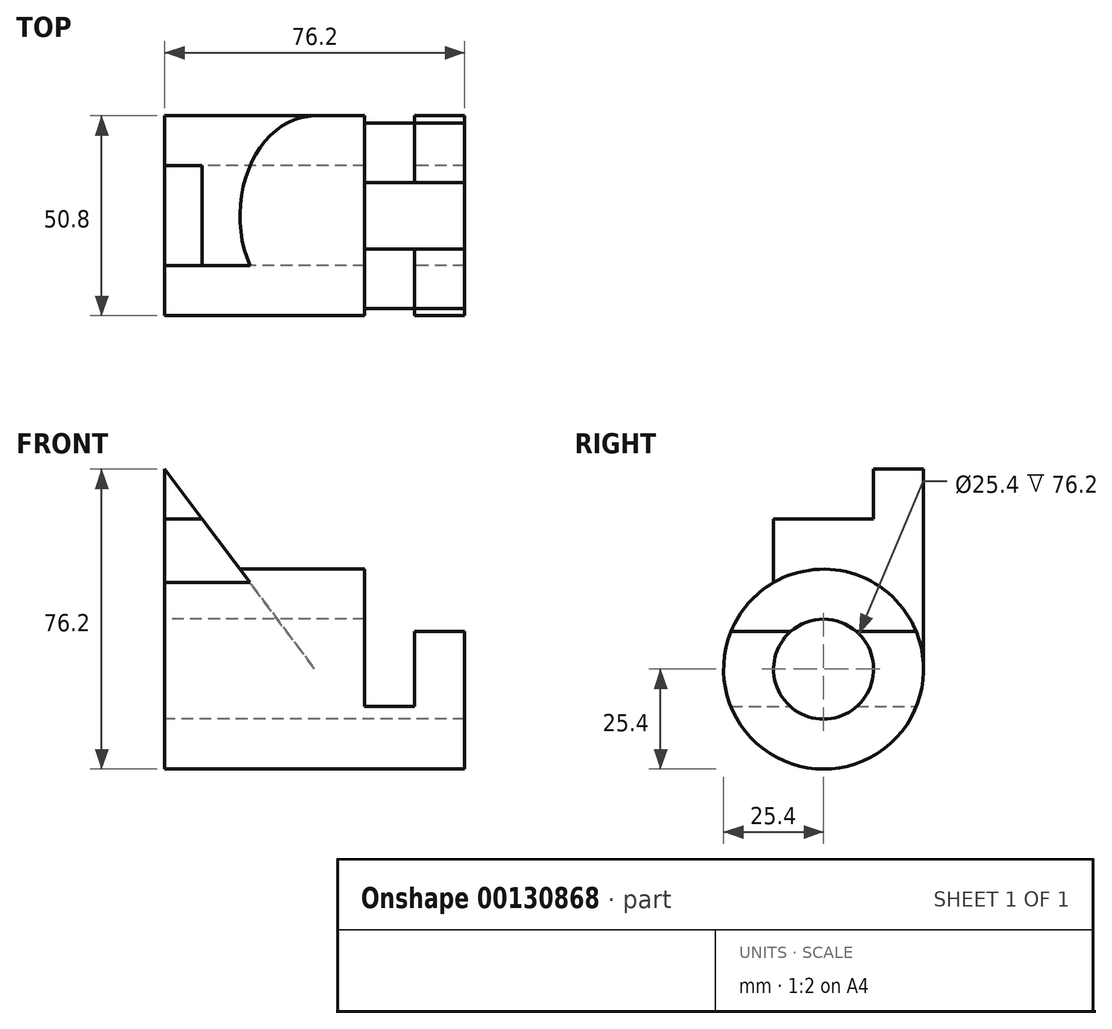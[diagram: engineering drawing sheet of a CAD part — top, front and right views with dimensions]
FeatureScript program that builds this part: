
annotation { "Feature Type Name" : "Feature", "Feature Type Description" : "" }
export const myFeature = defineFeature(function(context is Context, id is Id, definition is map)
    precondition{}
    {
        {
            var Q0;
            Q0=qCreatedBy(makeId("Right.planeOp"),FACE);
            var sketch = newSketch(context, id + "F0", { "sketchPlane" : qUnion([Q0])});
            skCircle(sketch, "E0", {"center": v(0, 0) * mm, "radius": 12.7 * mm});
            skCircle(sketch, "E1", {"center": v(0, 0) * mm, "radius": 25.4 * mm});
            skSolve(sketch);
        }
        {
            var Q0;
            Q0=qCreatedBy(makeId("Front.planeOp"),FACE);
            var sketch = newSketch(context, id + "F1", { "sketchPlane" : qUnion([Q0])});
            skLineSegment(sketch, "E2", {"start": v(0, 0) * mm, "end": v(0, 25.4) * mm, "construction": true});
            skLineSegment(sketch, "E3", {"start": v(0, 25.4) * mm, "end": v(50.8, 25.4) * mm, "construction": true});
            skLineSegment(sketch, "E4", {"start": v(50.8, 25.4) * mm, "end": v(50.8, -9.53) * mm});
            skLineSegment(sketch, "E5", {"start": v(50.8, -9.53) * mm, "end": v(63.5, -9.53) * mm});
            skLineSegment(sketch, "E6", {"start": v(63.5, -9.53) * mm, "end": v(63.5, 25.4) * mm});
            skLineSegment(sketch, "E7", {"start": v(63.5, 25.4) * mm, "end": v(50.8, 25.4) * mm});
            skSolve(sketch);
        }
        {
            var Q0;
            Q0=qCreatedBy(makeId("Front.planeOp"),FACE);
            var sketch = newSketch(context, id + "F2", { "sketchPlane" : qUnion([Q0])});
            skLineSegment(sketch, "E8", {"start": v(0, 0) * mm, "end": v(0, 50.8) * mm});
            skLineSegment(sketch, "E9", {"start": v(0, 0) * mm, "end": v(38.1, 0) * mm});
            skLineSegment(sketch, "E10", {"start": v(38.1, 0) * mm, "end": v(0, 50.8) * mm});
            skSolve(sketch);
        }
        {
            var Q0;
            Q0=qCreatedBy(makeId("Right.planeOp"),FACE);
            var sketch = newSketch(context, id + "F3", { "sketchPlane" : qUnion([Q0])});
            skLineSegment(sketch, "E11", {"start": v(0, 0) * mm, "end": v(25.4, 0) * mm, "construction": true});
            skLineSegment(sketch, "E12", {"start": v(0, 0) * mm, "end": v(-25.4, 0) * mm, "construction": true});
            skArc(sketch, "E13", {"start": v(25.4, 0) * mm, "mid": v(0, 25.4) * mm, "end": v(-25.4, 0) * mm});
            skLineSegment(sketch, "E14", {"start": v(-12.7, 38.1) * mm, "end": v(12.7, 38.1) * mm});
            skLineSegment(sketch, "E15.MirrorCS", {"start": v(12.7, 38.1) * mm, "end": v(-12.7, 38.1) * mm});
            skLineSegment(sketch, "E16.MirrorCS", {"start": v(12.7, 50.8) * mm, "end": v(12.7, 38.1) * mm});
            skLineSegment(sketch, "E17.MirrorCS", {"start": v(-12.7, 38.1) * mm, "end": v(-12.7, 22) * mm});
            skLineSegment(sketch, "E18.MirrorCS", {"start": v(-25.4, 0) * mm, "end": v(-25.4, 50.8) * mm});
            skLineSegment(sketch, "E19.MirrorCS", {"start": v(-25.4, 50.8) * mm, "end": v(12.7, 50.8) * mm});
            skSolve(sketch);
        }
        {
            var Q0;
            Q0 = qSketchRegion(id + "F2", true);
            extrude(context, id + "F4", {"entities" : qUnion([Q0]), "endBound" : BoundingType.SYMMETRIC, "depth" : 50.8 * mm});
        }
        {
            var Q0;
            Q0=makeQuery(id+"F3.imprint","IMPRINT",FACE,{"disambiguationData":[TD([[makeQuery(id+"F3.imprint","IMPRINT",EDGE,{"derivedFrom":sQuery(id+"F3.wireOp",EDGE,"E16.MirrorCS")}),-1.0]])]});
            extrude(context, id + "F5", {"entities" : qUnion([Q0]), "operationType" : NewBodyOperationType.REMOVE, "depth" : 50.8 * mm});
        }
        {
            var Q0;
            Q0=makeQuery(id+"F0.imprint","IMPRINT",FACE,{"disambiguationData":[TD([[makeQuery(id+"F0.imprint","IMPRINT",EDGE,{"derivedFrom":sQuery(id+"F0.wireOp",EDGE,"E0")}),-1.0]])]});
            extrude(context, id + "F6", {"entities" : qUnion([Q0]), "operationType" : NewBodyOperationType.ADD, "depth" : 76.2 * mm});
        }
        {
            var Q0;
            Q0=makeQuery(id+"F0.imprint","IMPRINT",FACE,{"disambiguationData":[TD([[makeQuery(id+"F0.imprint","IMPRINT",EDGE,{"derivedFrom":sQuery(id+"F0.wireOp",EDGE,"E0")}),1.0]])]});
            extrude(context, id + "F7", {"entities" : qUnion([Q0]), "operationType" : NewBodyOperationType.REMOVE, "depth" : 76.2 * mm});
        }
        {
            var Q0;
            Q0 = qSketchRegion(id + "F1", true);
            extrude(context, id + "F8", {"entities" : qUnion([Q0]), "operationType" : NewBodyOperationType.REMOVE, "endBound" : BoundingType.SYMMETRIC, "depth" : 50.8 * mm});
        }
        {
            var Q0;
            Q0=qCreatedBy(makeId("Front.planeOp"),FACE);
            var sketch = newSketch(context, id + "F9", { "sketchPlane" : qUnion([Q0])});
            skLineSegment(sketch, "E20", {"start": v(0, 0) * mm, "end": v(63.5, 0) * mm, "construction": true});
            skLineSegment(sketch, "E21", {"start": v(63.5, 0) * mm, "end": v(63.5, 25.4) * mm, "construction": true});
            skLineSegment(sketch, "E22", {"start": v(63.5, 25.4) * mm, "end": v(63.5, 9.53) * mm});
            skLineSegment(sketch, "E23", {"start": v(63.5, 9.53) * mm, "end": v(76.2, 9.53) * mm});
            skLineSegment(sketch, "E24", {"start": v(76.2, 9.53) * mm, "end": v(76.2, 25.4) * mm});
            skLineSegment(sketch, "E25", {"start": v(76.2, 25.4) * mm, "end": v(63.5, 25.4) * mm});
            skSolve(sketch);
        }
        {
            var Q0;
            Q0 = qSketchRegion(id + "F9", true);
            extrude(context, id + "F10", {"entities" : qUnion([Q0]), "operationType" : NewBodyOperationType.REMOVE, "endBound" : BoundingType.SYMMETRIC, "oppositeDirection" : true, "depth" : 50.8 * mm});
        }
    });
